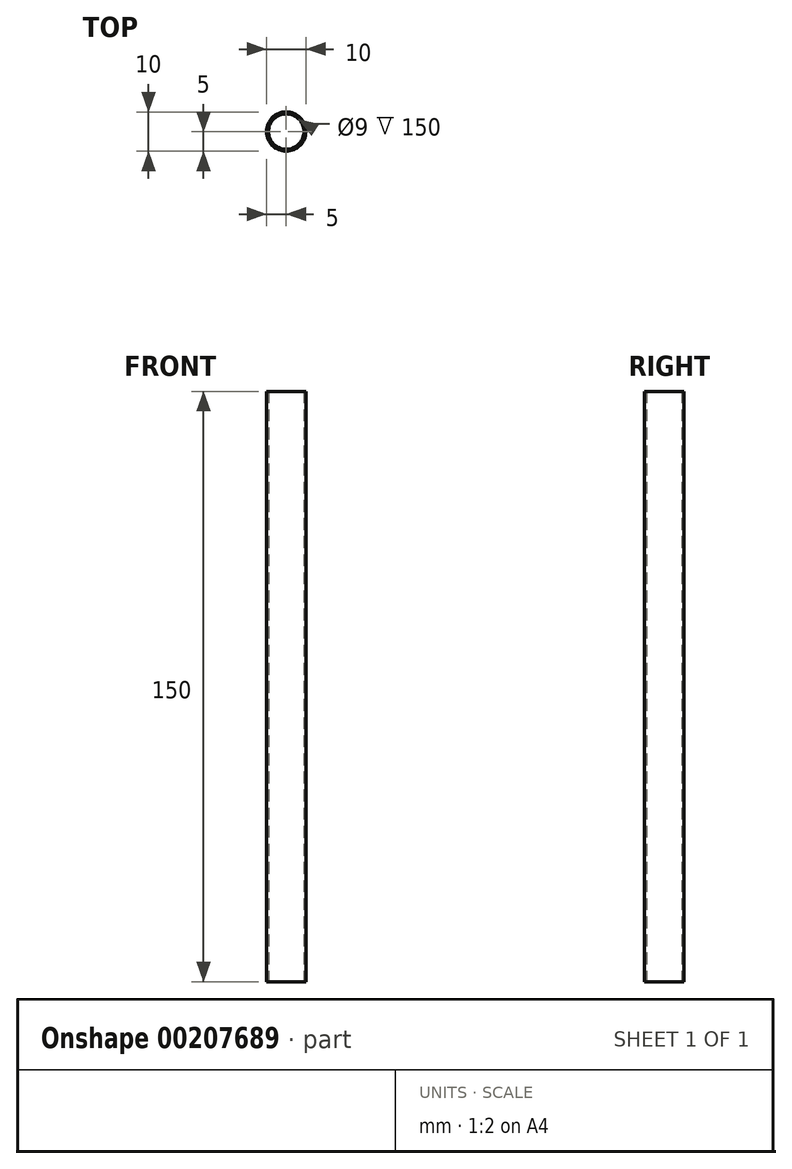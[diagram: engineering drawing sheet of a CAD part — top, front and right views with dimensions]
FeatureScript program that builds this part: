
annotation { "Feature Type Name" : "Feature", "Feature Type Description" : "" }
export const myFeature = defineFeature(function(context is Context, id is Id, definition is map)
    precondition{}
    {
        {
            var Q0;
            Q0=qCreatedBy(makeId("Top.planeOp"),FACE);
            var sketch = newSketch(context, id + "F0", { "sketchPlane" : qUnion([Q0])});
            skCircle(sketch, "E0", {"center": v(0, 0) * mm, "radius": 4.5 * mm});
            skCircle(sketch, "E1", {"center": v(0, 0) * mm, "radius": 5 * mm});
            skSolve(sketch);
        }
        {
            var Q0;
            Q0=makeQuery(id+"F0.imprint","IMPRINT",FACE,{"disambiguationData":[TD([[makeQuery(id+"F0.imprint","IMPRINT",EDGE,{"derivedFrom":sQuery(id+"F0.wireOp",EDGE,"E0")}),-1.0]])]});
            extrude(context, id + "F1", {"entities" : qUnion([Q0]), "endBound" : BoundingType.SYMMETRIC, "depth" : 150 * mm});
        }
    });
